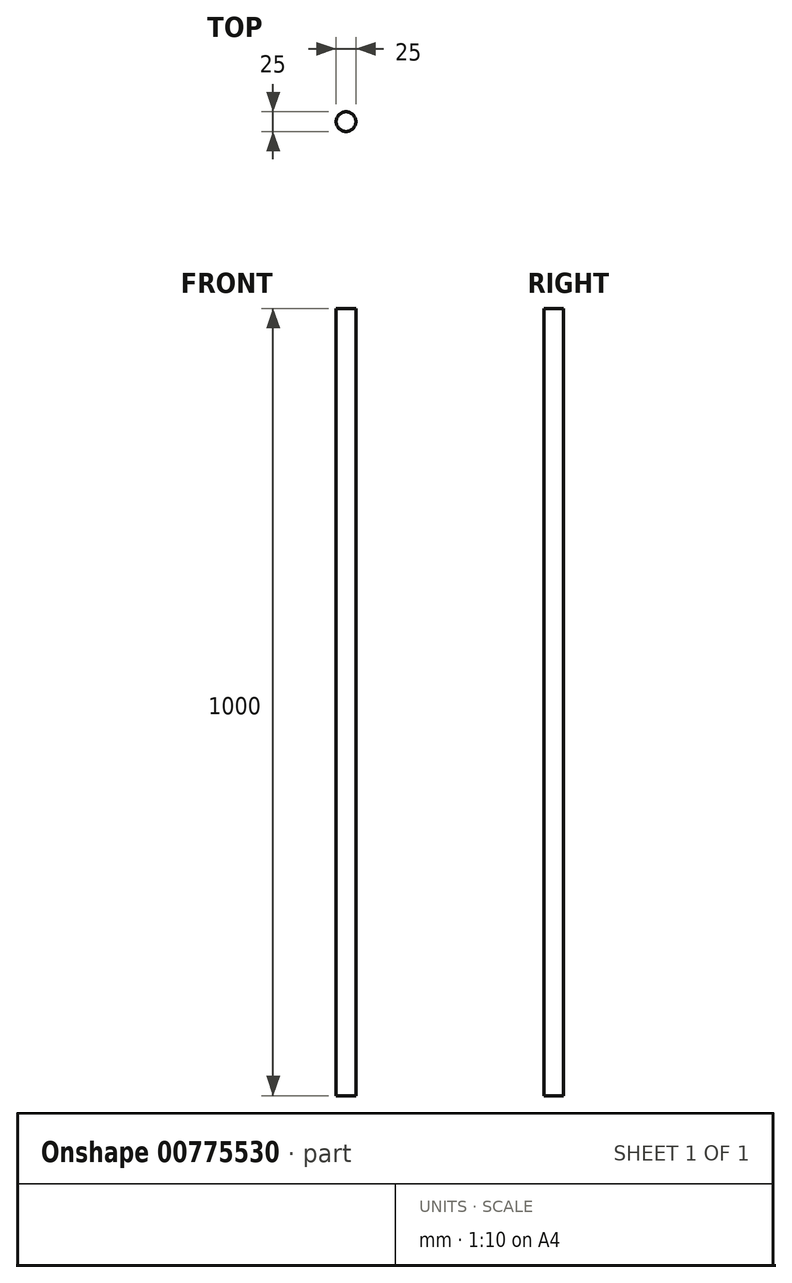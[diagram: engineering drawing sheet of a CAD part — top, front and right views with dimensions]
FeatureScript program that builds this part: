
annotation { "Feature Type Name" : "Feature", "Feature Type Description" : "" }
export const myFeature = defineFeature(function(context is Context, id is Id, definition is map)
    precondition{}
    {
        {
            var Q0;
            Q0=qCreatedBy(makeId("Top.planeOp"),FACE);
            var sketch = newSketch(context, id + "F0", { "sketchPlane" : qUnion([Q0])});
            skCircle(sketch, "E0", {"center": v(0, 0) * mm, "radius": 12.5 * mm});
            skSolve(sketch);
        }
        {
            var Q0;
            Q0 = qSketchRegion(id + "F0", true);
            extrude(context, id + "F1", {"entities" : qUnion([Q0]), "depth" : 1000 * mm, "offsetDistance" : 25.4 * mm});
        }
    });
